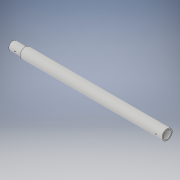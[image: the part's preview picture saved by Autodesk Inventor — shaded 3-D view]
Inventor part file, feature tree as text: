
AUTODESK INVENTOR PART (.ipt)
format: ipt  version: 2018 (Build 220112000, 112)  size: 136,192 bytes
history: native  units: in
note: dims shown in document units (in); Inventor stores cm internally (conversion verified against a paired STEP export)
features: sketch x4, extrude x3, fillet x1, plane x1, hole x1
ambient origin geometry x8: Origin, YZ Plane, XZ Plane, XY Plane, X Axis, Y Axis, Z Axis, Center Point
bodies: Solid1 (feature_tree)
feature tree (10):
  extrude  "Main Extursion"  Depth=10.0in
  fillet  "Fillet1"  Radius=899.9861in
  extrude  "Female"  Depth=149.9977in TaperAngle=0.0deg
  plane  "Work Plane1"
  extrude  "Male"  Depth=8.0in
  hole  "BoltHole"  [1 undecoded]
  sketch  "Sketch1"  dims[d0=1800.0in d1=10.0in d2=899.9861in]
  sketch  "Sketch2"  dims[d3=149.9977in d4=10.0in d5=0.0in]
  sketch  "Sketch3"  dims[d6=5.0in d7=8.0in]
  sketch  "Sketch4"  dims[d8=12.0in d9=0.0in d10=8.0in d11=12.0in d12=0.0in d13=1.0in d14=1.0in d15=6.0in d16=6.0in d17=0.865in d18=2.0in d19=0.375in d20=0.25in d21=0.5635in d22=2.625in d23=0.8108in]
note: 1 required parameter value undecoded (feature->parameter linkage not recoverable at this tier; creation-order binding heuristic only, values carry confidence <= 0.55)
